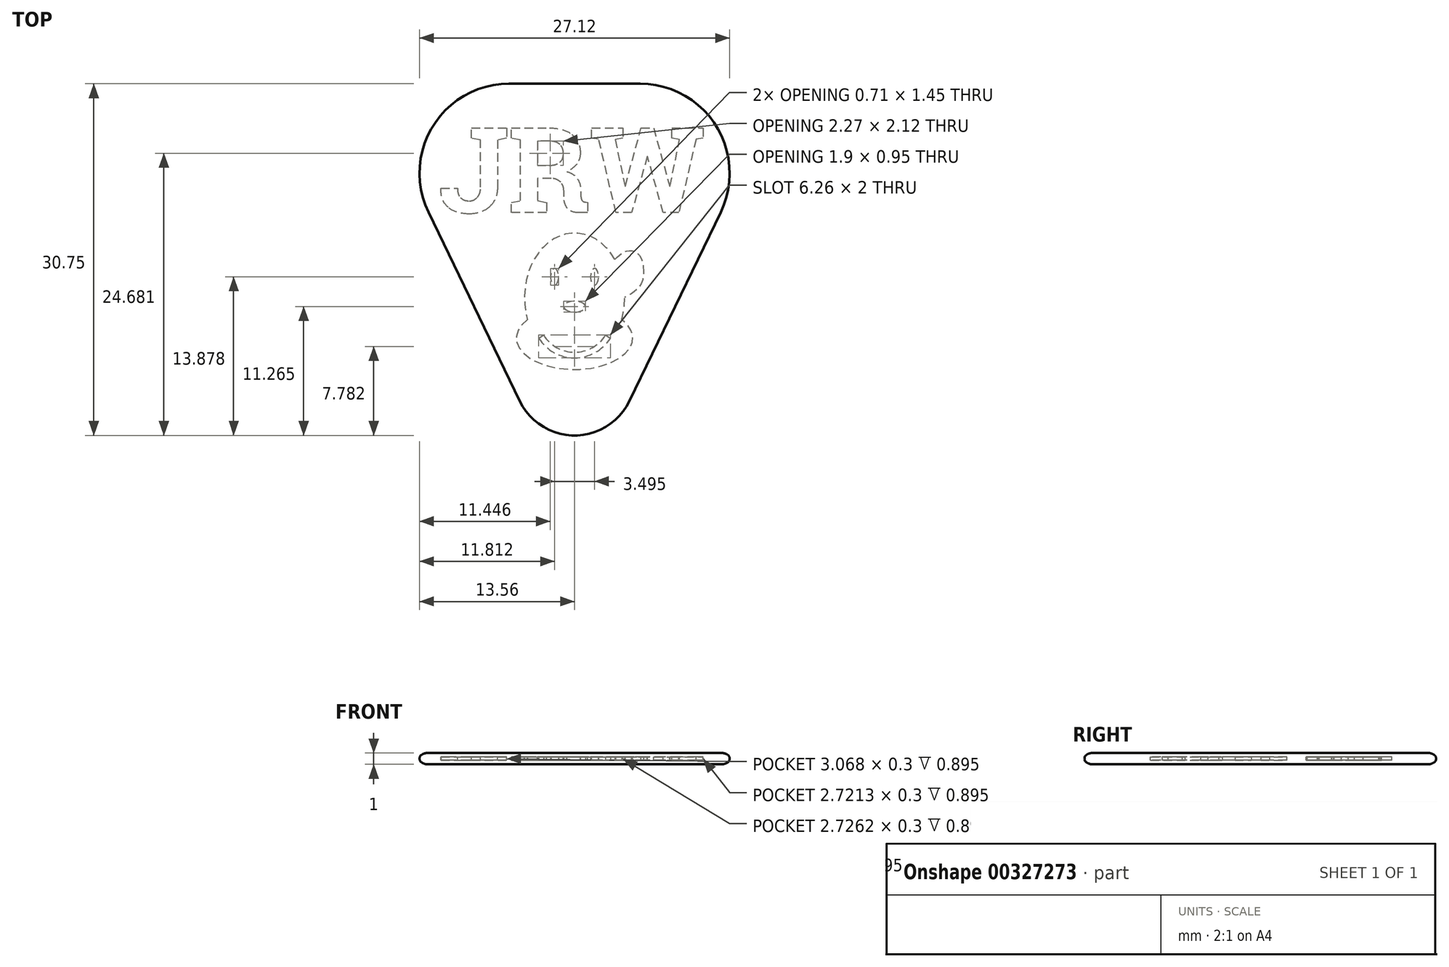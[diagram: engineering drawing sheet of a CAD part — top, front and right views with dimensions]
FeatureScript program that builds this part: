
annotation { "Feature Type Name" : "Feature", "Feature Type Description" : "" }
export const myFeature = defineFeature(function(context is Context, id is Id, definition is map)
    precondition{}
    {
        {
            var Q0;
            Q0=qCreatedBy(makeId("Top.planeOp"),FACE);
            var sketch = newSketch(context, id + "F0", { "sketchPlane" : qUnion([Q0])});
            skLineSegment(sketch, "E0", {"start": v(-5.74, 12.45) * mm, "end": v(5.74, 12.45) * mm});
            skLineSegment(sketch, "E1", {"start": v(12.95, 0.97) * mm, "end": v(4.95, -15.56) * mm});
            skLineSegment(sketch, "E2", {"start": v(-4.95, -15.56) * mm, "end": v(-12.95, 0.97) * mm});
            skPoint(sketch, "E3.visualSharp", {"position": v(-18.5, 12.45) * mm});
            skArc(sketch, "E3.filletArc", {"start": v(-5.74, 12.45) * mm, "mid": v(-12.52, 8.7) * mm, "end": v(-12.95, 0.97) * mm});
            skPoint(sketch, "E4.visualSharp", {"position": v(18.5, 12.45) * mm});
            skArc(sketch, "E4.filletArc", {"start": v(12.95, 0.97) * mm, "mid": v(12.52, 8.7) * mm, "end": v(5.74, 12.45) * mm});
            skPoint(sketch, "E5.visualSharp", {"position": v(0, -25.8) * mm});
            skArc(sketch, "E5.filletArc", {"start": v(-4.95, -15.56) * mm, "mid": v(0, -18.66) * mm, "end": v(4.95, -15.56) * mm});
            skSolve(sketch);
        }
        {
            var Q0;
            Q0=makeQuery(id+"F0.imprint","IMPRINT",FACE,{"disambiguationData":[TD([[makeQuery(id+"F0.imprint","IMPRINT",EDGE,{"derivedFrom":sQuery(id+"F0.wireOp",EDGE,"E0")}),-1.0]])]});
            extrude(context, id + "F1", {"entities" : qUnion([Q0]), "endBound" : BoundingType.SYMMETRIC, "depth" : 1 * mm, "offsetDistance" : 25 * mm});
        }
        {
            var Q0;
            Q0=makeQuery(id+"F1.opExtrude","CAP_EDGE",EDGE,{"disambiguationData":[OSD([sQuery(id+"F0.wireOp",EDGE,"E1")])],"isStart":false});
            var Q1;
            Q1=makeQuery(id+"F1.opExtrude","CAP_EDGE",EDGE,{"disambiguationData":[OSD([sQuery(id+"F0.wireOp",EDGE,"E1")])],"isStart":true});
            chamfer(context, id + "F2", {"entities" : qUnion([Q0, Q1]), "chamferType" : ChamferType.OFFSET_ANGLE, "width" : 0.5 * mm, "oppositeDirection" : false, "angle" : 45 * degree, "tangentPropagation" : true});
        }
        {
            var Q0;
            {var subQ0=sQuery(id+"F0.wireOp",EDGE,"E2");Q0=makeQuery(id+"F2.opChamfer","BLEND_EDGE",EDGE,{"blendedFrom":[makeQuery(id+"F1.opExtrude","CAP_EDGE",EDGE,{"disambiguationData":[OSD([subQ0])],"isStart":false}),makeQuery(id+"F1.opExtrude","CAP_FACE",FACE,{"disambiguationData":[OSD([sQuery(id+"F0.wireOp",EDGE,"E0"),sQuery(id+"F0.wireOp",EDGE,"E1"),subQ0,sQuery(id+"F0.wireOp",EDGE,"E3.filletArc"),sQuery(id+"F0.wireOp",EDGE,"E4.filletArc"),sQuery(id+"F0.wireOp",EDGE,"E5.filletArc")])],"isStart":false})],"blendedInto":[makeQuery(id+"F1.opExtrude","CAP_FACE",FACE,{"disambiguationData":[OSD([sQuery(id+"F0.wireOp",EDGE,"E0"),sQuery(id+"F0.wireOp",EDGE,"E1"),subQ0,sQuery(id+"F0.wireOp",EDGE,"E3.filletArc"),sQuery(id+"F0.wireOp",EDGE,"E4.filletArc"),sQuery(id+"F0.wireOp",EDGE,"E5.filletArc")])],"isStart":false})]});}
            var Q1;
            {var subQ0=sQuery(id+"F0.wireOp",EDGE,"E1");Q1=makeQuery(id+"F2.opChamfer","BLEND_EDGE",EDGE,{"blendedFrom":[makeQuery(id+"F1.opExtrude","CAP_EDGE",EDGE,{"disambiguationData":[OSD([subQ0])],"isStart":true}),makeQuery(id+"F1.opExtrude","CAP_FACE",FACE,{"disambiguationData":[OSD([sQuery(id+"F0.wireOp",EDGE,"E0"),subQ0,sQuery(id+"F0.wireOp",EDGE,"E2"),sQuery(id+"F0.wireOp",EDGE,"E3.filletArc"),sQuery(id+"F0.wireOp",EDGE,"E4.filletArc"),sQuery(id+"F0.wireOp",EDGE,"E5.filletArc")])],"isStart":true})],"blendedInto":[makeQuery(id+"F1.opExtrude","CAP_FACE",FACE,{"disambiguationData":[OSD([sQuery(id+"F0.wireOp",EDGE,"E0"),subQ0,sQuery(id+"F0.wireOp",EDGE,"E2"),sQuery(id+"F0.wireOp",EDGE,"E3.filletArc"),sQuery(id+"F0.wireOp",EDGE,"E4.filletArc"),sQuery(id+"F0.wireOp",EDGE,"E5.filletArc")])],"isStart":true})]});}
            fillet(context, id + "F3", {"entities" : qUnion([Q0, Q1]), "radius" : 1 * mm, "tangentPropagation" : true, "allowEdgeOverflow" : false});
        }
        {
            var Q0;
            Q0=qCreatedBy(makeId("Top.planeOp"),FACE);
            var sketch = newSketch(context, id + "F4", { "sketchPlane" : qUnion([Q0])});
            skText(sketch, "E6", { "text": "JRW", "fontName": "RobotoSlab-Bold.ttf"});
            const initialGuessF4  = {"E6": [-0.01187, 0.001, 1, 0, 0.0075]};
            skSetInitialGuess(sketch, initialGuessF4);
            skSolve(sketch);
        }
        {
            var Q0;
            Q0=qSketchRegion(id+"F4",true);
            var Q1;
            Q1 = qSketchRegion(id + "F7", true);
            extrude(context, id + "F5", {"entities" : qUnion([Q0, Q1]), "operationType" : NewBodyOperationType.REMOVE, "endBound" : BoundingType.SYMMETRIC, "oppositeDirection" : true, "depth" : 0.3 * mm, "offsetDistance" : 25 * mm});
        }
        {
            var Q0;
            {var subQ0=sQuery(id+"F0.wireOp",EDGE,"E2");Q0=makeQuery(id+"F2.opChamfer","BLEND_EDGE",EDGE,{"blendedFrom":[makeQuery(id+"F1.opExtrude","CAP_EDGE",EDGE,{"disambiguationData":[OSD([subQ0])],"isStart":true}),makeQuery(id+"F1.opExtrude","CAP_EDGE",EDGE,{"disambiguationData":[OSD([subQ0])],"isStart":false})],"blendedInto":[]});}
            fillet(context, id + "F6", {"entities" : qUnion([Q0]), "radius" : 0.4 * mm, "tangentPropagation" : true, "allowEdgeOverflow" : false});
        }
        {
            var Q0;
            Q0=qCreatedBy(makeId("Top.planeOp"),FACE);
            var sketch = newSketch(context, id + "F7", { "sketchPlane" : qUnion([Q0])});
            skEllipticalArc(sketch, "E7", {});
            skEllipticalArc(sketch, "E8", {});
            skFitSpline(sketch, "E9", {"points": [v(3.52, -3.07) * mm, v(4.55, -2.36) * mm, v(5.62, -2.67) * mm, v(5.88, -5.07) * mm, v(4.38, -6.42) * mm], "startDerivative": vector(4.44, 4.1) * mm, "endDerivative": vector(-6.73, -3.64) * mm});
            skFitSpline(sketch, "E10.MirrorCS", {"points": [v(-3.52, -3.07) * mm, v(-4.55, -2.36) * mm, v(-5.62, -2.67) * mm, v(-5.88, -5.07) * mm, v(-4.38, -6.42) * mm], "startDerivative": vector(-4.44, 4.1) * mm, "endDerivative": vector(6.73, -3.64) * mm});
            skEllipse(sketch, "E11", {"center": v(1.75, -4.6) * mm, "majorRadius": 0.72 * mm, "minorRadius": 0.36 * mm, "majorAxis": v(0, -1)});
            skEllipse(sketch, "E12", {"center": v(0, -7.21) * mm, "majorRadius": 0.95 * mm, "minorRadius": 0.47 * mm, "majorAxis": v(1, 0)});
            skEllipse(sketch, "E13.MirrorC", {"center": v(-1.75, -4.6) * mm, "majorRadius": 0.72 * mm, "minorRadius": 0.36 * mm, "majorAxis": v(0, -1)});
            skFitSpline(sketch, "E14", {"points": [v(0, -3.07) * mm, v(-1.55, -2.7) * mm, v(-2.93, -3.6) * mm, v(-2.7, -7.63) * mm], "startDerivative": vector(-5.51, 2.21) * mm, "endDerivative": vector(2.18, -10.68) * mm});
            skFitSpline(sketch, "E15.MirrorCS", {"points": [v(0, -3.07) * mm, v(1.55, -2.7) * mm, v(2.93, -3.6) * mm, v(2.7, -7.63) * mm], "startDerivative": vector(5.51, 2.21) * mm, "endDerivative": vector(-2.18, -10.68) * mm});
            skArc(sketch, "E16", {"start": v(3.13, -9.96) * mm, "mid": v(1.8, -11.24) * mm, "end": v(0, -11.7) * mm});
            skArc(sketch, "E17.MirrorCS", {"start": v(-3.13, -9.96) * mm, "mid": v(-1.8, -11.24) * mm, "end": v(0, -11.7) * mm});
            skArc(sketch, "E18.0", {"start": v(-2.7, -9.7) * mm, "mid": v(-1.55, -10.8) * mm, "end": v(0, -11.2) * mm});
            skArc(sketch, "E19.MirrorCS", {"start": v(2.7, -9.7) * mm, "mid": v(1.55, -10.8) * mm, "end": v(0, -11.2) * mm});
            skLineSegment(sketch, "E20", {"start": v(-3.13, -9.96) * mm, "end": v(-2.7, -9.7) * mm});
            skLineSegment(sketch, "E21", {"start": v(2.7, -9.7) * mm, "end": v(3.13, -9.96) * mm});
            skFitSpline(sketch, "E22.0", {"points": [v(-0.98, -12.45) * mm, v(0, -12.58) * mm, v(0.98, -12.45) * mm, v(1.91, -12.1) * mm, v(2.77, -11.5) * mm, v(3.5, -10.73) * mm, v(4.1, -9.8) * mm, v(4.53, -8.73) * mm, v(4.8, -7.6) * mm, v(4.89, -6.42) * mm, v(4.8, -5.24) * mm, v(4.53, -4.1) * mm, v(4.1, -3.04) * mm, v(3.5, -2.11) * mm, v(2.77, -1.33) * mm, v(1.91, -0.75) * mm, v(0.98, -0.38) * mm, v(0, -0.26) * mm, v(-0.98, -0.38) * mm, v(-1.91, -0.75) * mm, v(-2.77, -1.33) * mm, v(-3.5, -2.11) * mm, v(-4.1, -3.04) * mm, v(-4.53, -4.1) * mm, v(-4.8, -5.24) * mm, v(-4.89, -6.42) * mm, v(-4.8, -7.6) * mm, v(-4.53, -8.73) * mm, v(-4.1, -9.8) * mm, v(-3.5, -10.73) * mm, v(-2.77, -11.5) * mm, v(-1.91, -12.1) * mm, v(-0.98, -12.45) * mm, v(0, -12.58) * mm, v(0.98, -12.45) * mm]});
            skLineSegment(sketch, "E23", {"start": v(-4.58, -8.46) * mm, "end": v(-4.51, -8.7) * mm});
            skLineSegment(sketch, "E24.MirrorCS", {"start": v(4.58, -8.46) * mm, "end": v(4.51, -8.7) * mm});
            const initialGuessF7  = {"E7": [1.3970180617363381e-08, -0.006418291775050674, 0, -1, 0.005639855284243822, 0.0043772660306950735, 1.2220849475554956, 5.061097125015299], "E8": [0, -0.009961281454055101, 1, 0, 0.005087355151772499, 0.002746738975732119, 2.1312338919539324, 1.0103587616358605]};
            skSetInitialGuess(sketch, initialGuessF7);
            skSolve(sketch);
        }
        {
            var Q0;
            Q0=qSketchRegion(id+"F7",true);
            var Q1;
            Q1=makeQuery(id+"F7.imprint","IMPRINT",FACE,{"disambiguationData":[TD([[makeQuery(id+"F7.imprint","IMPRINT",EDGE,{"derivedFrom":sQuery(id+"F7.wireOp",EDGE,"939ed108-b3df-4f31-88ce-246f36476dcc.0")}),-1.0]])]});
            var Q2;
            Q2=makeQuery(id+"F7.imprint","IMPRINT",FACE,{"disambiguationData":[TD([[makeQuery(id+"F7.imprint","IMPRINT",EDGE,{"derivedFrom":sQuery(id+"F7.wireOp",EDGE,"7208b4ee-4551-4fd0-8a5f-77d057b4d0f6.0")}),-1.0]])]});
            extrude(context, id + "F8", {"entities" : qUnion([Q0, Q1, Q2]), "operationType" : NewBodyOperationType.REMOVE, "endBound" : BoundingType.SYMMETRIC, "depth" : 0.3 * mm, "offsetDistance" : 25 * mm});
        }
    });
